# Revit family: P190780JX-197c_JKTPX151HM_StainlessSteel_JA_Dish_Trash_Compactors_FINAL
name_source: partatom
category: Specialty Equipment
units: mm (PartAtom-declared; Revit-internal decimal feet)

## family parameters
Always vertical = Yes
Cut with Voids When Loaded = No
Enable Cutting in Views = No
Maintain Annotation Orientation = No
Part Type = Normal
Room Calculation Point = No
Round Connector Dimension = Use Diameter
Shared = No
Work Plane-Based = No

## types (1)
- JKTPX151HM
    Accent Material = ARCAT - Metal - Steel - Stainless
    Amps = 0 A
    Body Material = ARCAT - Plastic, ABS - Black
    Bottom Panel = ARCAT - Plastic, ABS - Black
    Clearance Material = ARCAT - Clearance
    Default Elevation = 0"
    Depth = 24"
    Description = NOIR™ 15" Trash Compactor Panel Kit
Trousse de panneau pour compacteur de déchets NOIR™, 15 po
    Dimension Guide = https://www.whirlpool.com
https://www.whirlpool.com
    Door Material = ARCAT - Metal - Steel - Stainless
    Family Name = TRASH COMPACTOR PANEL KITS NOIR
    Feature 1 = Stainless Steel Door, NOIR™ styling
Porte en acier inoxydable, style NOIR™
    Handle Material = ARCAT - Metal - Steel - Gray
    Height = 34 1/8"
    Manufacturer = Jenn Air
    Model = JKTPX151HM
    Voltage = 0 V
    Width = 14 7/8"

## geometry (parser evidence)
native form markers: Sweep x2
no freeform markers — native parametric forms only
